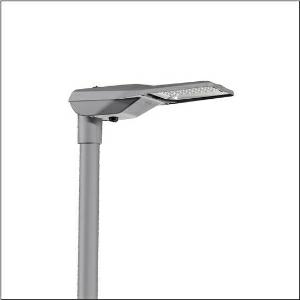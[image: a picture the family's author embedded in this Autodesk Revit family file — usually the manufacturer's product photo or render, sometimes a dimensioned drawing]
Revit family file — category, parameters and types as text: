
# Revit family: streetlight_sl_21_iq_mini___st1_0a_5xe2d41y08jb_7656
name_source: partatom
category: Lighting Fixtures
units: mm (PartAtom-declared; Revit-internal decimal feet)

## family parameters
Cut with Voids When Loaded = No
Host = Face
Light Source = No
Part Type = Normal
Room Calculation Point = No
Round Connector Dimension = Use Diameter
Shared = No

## types (1)
- --- (1 x LED, 11600 lm, 72.5 W, 4000K)
    Apparent Load = 73 VA
    CIE Flux Codes = 40 73 97 100 100
    Color Rendering = 70
    Color Temperature = 4000K
    Default Elevation = 1800 mm
    Description = Streetlight SL 21 iQ mini, mast luminaire, primary light control with lens, of PMMA, primary optical cover: cover, of toughened safety glass, transparent, light distribution: ST1.0a, light emission: direct distribution, primary light characteristic: asymmetric, installation type: post-top, side-entry, LED, High Power LED, rated luminous flux: 11.600lm, luminous efficacy: 160lm/W, light colour: 740, colour temperature: 4000K, control gear: iQ-Street Remote, D4i with power reduction, control: pre-setting: logarithmic dimming characteristic, Street-Remote, Auto-Match, Temp-Guard, Lumen-Switch, Night-Set, Smart-Wire, Light-Fading, Desk-Remote (wireless, voltage-free reading and setting of iQ features in the workshop via application-optimized NFC function/RFID function), optimised constant luminous flux control (CLO 2.0), mains connection: 220..240V, AC, 50/60Hz, start of lifetime: 73W, end of service life: 76W, reduction: 33W, luminaire housing, of diecast aluminium, powder-coated, Siteco® metallic grey (DB 702S), corrosivity category C5 mid according to DIN EN ISO 12944, please order mast flange separately, inclination adjustable: 0°, 5°, 10°, 15°, sealing non-destructively replaceable, multi-level sealing system, length: 628mm, width: 235mm, height: 110mm, mast flange for spigot size: 42mm (side-entry): 5XC10008XM4, 60/48mm (side-entry/post-top): 5XC10108XM2, 76/60mm (side-entry/post-top): 5XC10108XM1, mounting height: 4..8m, Smart Interface below and above, protection rating (complete): IP66, insulation class (complete): insulation class II (safety insulation), certification: CE, ENEC, ENEC+, VDE, impact resistance: IK10, permissible operating ambient temperature for outdoor applications: -40..+50°C, standard-compliant lighting for roads and squares, packaging unit: 1 piece

Light Distribution: ST1.0a
    Height = 110 mm
    Lamp = 1 x LED
    Lamp Light Flux = 11600 lm
    Lamp Power = 72.5 W
    Lamp count = 1
    Length = 625 mm
    Luminous efficacy = 160 lm/W
    Manufacturer = Siteco
    ModVariant = No
    Model = 5XE2D41Y08JB
    Number of Poles = 1
    OnlyDefault = Yes
    Power Factor = 1
    Product Name = Streetlight SL 21 iQ mini | ST1.0a
    Product group = mast luminaire | pylon top
    ProductGroupID = 6100
    Protection Class = Protection class II
    Protection Degree = IP 66
    RLX_Detail_Level = 1
    RLX_Emergency_Light_Flux = 0 lm
    RLX_Emergency_Type = 0
    RLX_Emergency_Type_DB = No
    RlxData = <blob elided: 26585 chars, md5=3a23402a>
    Socket = socket
    Standby Power = 0 W
    System Light Flux = 11600 lm
    System Power = 73 W
    Type Comments = factory setting: luminous flux: 100 % | dim-lin: 254 | 755 mA
    Type Image = l_1003514.jpg
    URL = http://relux.com
    VarID = @adj_113996
    Voltage = 0 V
    Weight = 0.00 kg
    Width = 234 mm

## geometry (parser evidence)
native form markers: Blend x4, Sweep x11
no freeform markers — native parametric forms only
